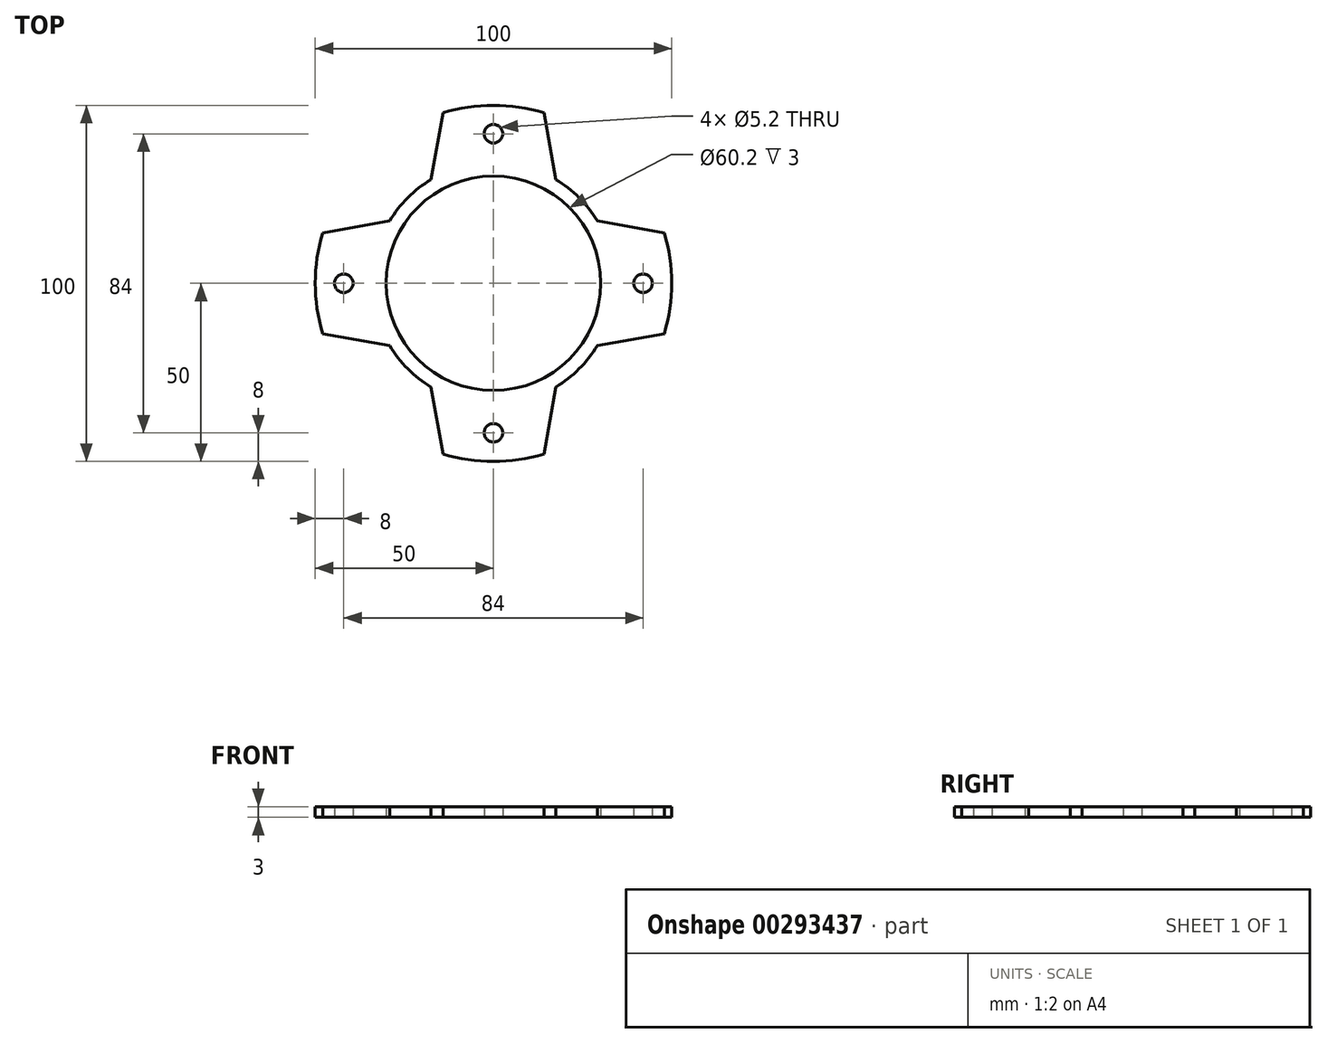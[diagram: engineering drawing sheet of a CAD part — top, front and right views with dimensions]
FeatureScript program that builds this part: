
annotation { "Feature Type Name" : "Feature", "Feature Type Description" : "" }
export const myFeature = defineFeature(function(context is Context, id is Id, definition is map)
    precondition{}
    {
        {
            var Q0;
            Q0=qCreatedBy(makeId("Top.planeOp"),FACE);
            var sketch = newSketch(context, id + "F0", { "sketchPlane" : qUnion([Q0])});
            skCircle(sketch, "E0", {"center": v(0, 0) * mm, "radius": 30.1 * mm});
            skCircle(sketch, "E1", {"center": v(0, 0) * mm, "radius": 34 * mm});
            skCircle(sketch, "E2", {"center": v(0, 0) * mm, "radius": 50 * mm});
            skCircle(sketch, "E3", {"center": v(-42, 0) * mm, "radius": 2.6 * mm});
            skCircle(sketch, "E4", {"center": v(42, 0) * mm, "radius": 2.6 * mm});
            skCircle(sketch, "E5", {"center": v(0, 42) * mm, "radius": 2.6 * mm});
            skCircle(sketch, "E6", {"center": v(0, -42) * mm, "radius": 2.6 * mm});
            skCircle(sketch, "E7", {"center": v(-42, 0) * mm, "radius": 15 * mm});
            skCircle(sketch, "E8", {"center": v(0, 42) * mm, "radius": 15 * mm});
            skCircle(sketch, "E9", {"center": v(42, 0) * mm, "radius": 15 * mm});
            skCircle(sketch, "E10", {"center": v(0, -42) * mm, "radius": 15 * mm});
            skLineSegment(sketch, "E11", {"start": v(-17.5, -29.15) * mm, "end": v(-10.6, -68.26) * mm});
            skLineSegment(sketch, "E12", {"start": v(-29.15, 17.5) * mm, "end": v(-64.19, 11.32) * mm});
            skLineSegment(sketch, "E13", {"start": v(-29.15, -17.5) * mm, "end": v(-69.22, -10.43) * mm});
            skLineSegment(sketch, "E14", {"start": v(-17.5, 29.15) * mm, "end": v(-10.72, 67.6) * mm});
            skLineSegment(sketch, "E15", {"start": v(29.15, 17.5) * mm, "end": v(70.35, 10.23) * mm});
            skLineSegment(sketch, "E16", {"start": v(29.15, -17.5) * mm, "end": v(61.9, -11.72) * mm});
            skLineSegment(sketch, "E17", {"start": v(17.5, -29.15) * mm, "end": v(11.2, -64.88) * mm});
            skLineSegment(sketch, "E18", {"start": v(17.5, 29.15) * mm, "end": v(10.52, 68.74) * mm});
            skSolve(sketch);
        }
        {
            var Q0;
            {var subQ5=sQuery(id+"F0.wireOp",EDGE,"E8");var subQ6=sQuery(id+"F0.wireOp",EDGE,"E0");var subQ7=makeQuery(id+"F0.imprint","INTERSECT",VERTEX,{"disambiguationData":[OD(1.0)],"derivedFrom":[subQ6,subQ5]});Q0=makeQuery(id+"F0.imprint","IMPRINT",FACE,{"disambiguationData":[TD([[makeQuery(id+"F0.imprint","IMPRINT",EDGE,{"disambiguationData":[TD([[subQ7,-1.0]])],"derivedFrom":subQ6}),-1.0]])]});}
            var Q1;
            {var subQ0=sQuery(id+"F0.wireOp",EDGE,"E14");var subQ1=sQuery(id+"F0.wireOp",EDGE,"E1");var subQ2=makeQuery(id+"F0.imprint","INTERSECT",VERTEX,{"derivedFrom":[subQ1,subQ0]});Q1=makeQuery(id+"F0.imprint","IMPRINT",FACE,{"disambiguationData":[TD([[makeQuery(id+"F0.imprint","IMPRINT",EDGE,{"disambiguationData":[TD([[subQ2,1.0]])],"derivedFrom":subQ1}),-1.0]])]});}
            var Q2;
            Q2=makeQuery(id+"F0.imprint","IMPRINT",FACE,{"disambiguationData":[TD([[makeQuery(id+"F0.imprint","IMPRINT",EDGE,{"derivedFrom":sQuery(id+"F0.wireOp",EDGE,"E5")}),-1.0]])]});
            var Q3;
            {var subQ0=sQuery(id+"F0.wireOp",EDGE,"E18");var subQ1=sQuery(id+"F0.wireOp",EDGE,"E1");var subQ2=makeQuery(id+"F0.imprint","INTERSECT",VERTEX,{"derivedFrom":[subQ1,subQ0]});Q3=makeQuery(id+"F0.imprint","IMPRINT",FACE,{"disambiguationData":[TD([[makeQuery(id+"F0.imprint","IMPRINT",EDGE,{"disambiguationData":[TD([[subQ2,-1.0]])],"derivedFrom":subQ1}),-1.0]])]});}
            var Q4;
            {var subQ0=sQuery(id+"F0.wireOp",EDGE,"E8");var subQ1=sQuery(id+"F0.wireOp",EDGE,"E0");var subQ2=makeQuery(id+"F0.imprint","INTERSECT",VERTEX,{"disambiguationData":[OD(0.0)],"derivedFrom":[subQ1,subQ0]});Q4=makeQuery(id+"F0.imprint","IMPRINT",FACE,{"disambiguationData":[TD([[makeQuery(id+"F0.imprint","IMPRINT",EDGE,{"disambiguationData":[TD([[subQ2,-1.0]])],"derivedFrom":subQ1}),-1.0]])]});}
            var Q5;
            {var subQ5=sQuery(id+"F0.wireOp",EDGE,"E8");var subQ7=sQuery(id+"F0.wireOp",EDGE,"E0");var subQ8=makeQuery(id+"F0.imprint","INTERSECT",VERTEX,{"disambiguationData":[OD(0.0)],"derivedFrom":[subQ7,subQ5]});Q5=makeQuery(id+"F0.imprint","IMPRINT",FACE,{"disambiguationData":[TD([[makeQuery(id+"F0.imprint","IMPRINT",EDGE,{"disambiguationData":[TD([[subQ8,1.0]])],"derivedFrom":subQ7}),-1.0]])]});}
            var Q6;
            {var subQ0=sQuery(id+"F0.wireOp",EDGE,"E15");var subQ1=sQuery(id+"F0.wireOp",EDGE,"E1");var subQ2=makeQuery(id+"F0.imprint","INTERSECT",VERTEX,{"derivedFrom":[subQ1,subQ0]});Q6=makeQuery(id+"F0.imprint","IMPRINT",FACE,{"disambiguationData":[TD([[makeQuery(id+"F0.imprint","IMPRINT",EDGE,{"disambiguationData":[TD([[subQ2,1.0]])],"derivedFrom":subQ1}),-1.0]])]});}
            var Q7;
            Q7=makeQuery(id+"F0.imprint","IMPRINT",FACE,{"disambiguationData":[TD([[makeQuery(id+"F0.imprint","IMPRINT",EDGE,{"derivedFrom":sQuery(id+"F0.wireOp",EDGE,"E4")}),-1.0]])]});
            var Q8;
            {var subQ0=sQuery(id+"F0.wireOp",EDGE,"E14");var subQ1=sQuery(id+"F0.wireOp",EDGE,"E2");var subQ2=makeQuery(id+"F0.imprint","INTERSECT",VERTEX,{"derivedFrom":[subQ1,subQ0]});Q8=makeQuery(id+"F0.imprint","IMPRINT",FACE,{"disambiguationData":[TD([[makeQuery(id+"F0.imprint","IMPRINT",EDGE,{"disambiguationData":[TD([[subQ2,1.0]])],"derivedFrom":subQ1}),1.0]])]});}
            var Q9;
            {var subQ0=sQuery(id+"F0.wireOp",EDGE,"E18");var subQ1=sQuery(id+"F0.wireOp",EDGE,"E2");var subQ2=makeQuery(id+"F0.imprint","INTERSECT",VERTEX,{"derivedFrom":[subQ1,subQ0]});Q9=makeQuery(id+"F0.imprint","IMPRINT",FACE,{"disambiguationData":[TD([[makeQuery(id+"F0.imprint","IMPRINT",EDGE,{"disambiguationData":[TD([[subQ2,-1.0]])],"derivedFrom":subQ1}),1.0]])]});}
            var Q10;
            {var subQ0=sQuery(id+"F0.wireOp",EDGE,"E16");var subQ1=sQuery(id+"F0.wireOp",EDGE,"E1");var subQ2=makeQuery(id+"F0.imprint","INTERSECT",VERTEX,{"derivedFrom":[subQ1,subQ0]});Q10=makeQuery(id+"F0.imprint","IMPRINT",FACE,{"disambiguationData":[TD([[makeQuery(id+"F0.imprint","IMPRINT",EDGE,{"disambiguationData":[TD([[subQ2,-1.0]])],"derivedFrom":subQ1}),-1.0]])]});}
            var Q11;
            {var subQ5=sQuery(id+"F0.wireOp",EDGE,"E10");var subQ7=sQuery(id+"F0.wireOp",EDGE,"E0");var subQ9=makeQuery(id+"F0.imprint","INTERSECT",VERTEX,{"disambiguationData":[OD(1.0)],"derivedFrom":[subQ7,subQ5]});Q11=makeQuery(id+"F0.imprint","IMPRINT",FACE,{"disambiguationData":[TD([[makeQuery(id+"F0.imprint","IMPRINT",EDGE,{"disambiguationData":[TD([[subQ9,-1.0]])],"derivedFrom":subQ7}),-1.0]])]});}
            var Q12;
            {var subQ0=sQuery(id+"F0.wireOp",EDGE,"E9");var subQ1=sQuery(id+"F0.wireOp",EDGE,"E0");var subQ2=makeQuery(id+"F0.imprint","INTERSECT",VERTEX,{"disambiguationData":[OD(0.0)],"derivedFrom":[subQ1,subQ0]});Q12=makeQuery(id+"F0.imprint","IMPRINT",FACE,{"disambiguationData":[TD([[makeQuery(id+"F0.imprint","IMPRINT",EDGE,{"disambiguationData":[TD([[subQ2,1.0]])],"derivedFrom":subQ1}),-1.0]])]});}
            var Q13;
            {var subQ0=sQuery(id+"F0.wireOp",EDGE,"E16");var subQ1=sQuery(id+"F0.wireOp",EDGE,"E2");var subQ2=makeQuery(id+"F0.imprint","INTERSECT",VERTEX,{"derivedFrom":[subQ1,subQ0]});Q13=makeQuery(id+"F0.imprint","IMPRINT",FACE,{"disambiguationData":[TD([[makeQuery(id+"F0.imprint","IMPRINT",EDGE,{"disambiguationData":[TD([[subQ2,-1.0]])],"derivedFrom":subQ1}),1.0]])]});}
            var Q14;
            {var subQ0=sQuery(id+"F0.wireOp",EDGE,"E15");var subQ1=sQuery(id+"F0.wireOp",EDGE,"E2");var subQ2=makeQuery(id+"F0.imprint","INTERSECT",VERTEX,{"derivedFrom":[subQ1,subQ0]});Q14=makeQuery(id+"F0.imprint","IMPRINT",FACE,{"disambiguationData":[TD([[makeQuery(id+"F0.imprint","IMPRINT",EDGE,{"disambiguationData":[TD([[subQ2,1.0]])],"derivedFrom":subQ1}),1.0]])]});}
            var Q15;
            {var subQ0=sQuery(id+"F0.wireOp",EDGE,"E10");var subQ1=sQuery(id+"F0.wireOp",EDGE,"E0");var subQ2=makeQuery(id+"F0.imprint","INTERSECT",VERTEX,{"disambiguationData":[OD(0.0)],"derivedFrom":[subQ1,subQ0]});Q15=makeQuery(id+"F0.imprint","IMPRINT",FACE,{"disambiguationData":[TD([[makeQuery(id+"F0.imprint","IMPRINT",EDGE,{"disambiguationData":[TD([[subQ2,-1.0]])],"derivedFrom":subQ1}),-1.0]])]});}
            var Q16;
            Q16=makeQuery(id+"F0.imprint","IMPRINT",FACE,{"disambiguationData":[TD([[makeQuery(id+"F0.imprint","IMPRINT",EDGE,{"derivedFrom":sQuery(id+"F0.wireOp",EDGE,"E6")}),-1.0]])]});
            var Q17;
            {var subQ0=sQuery(id+"F0.wireOp",EDGE,"E11");var subQ1=sQuery(id+"F0.wireOp",EDGE,"E1");var subQ2=makeQuery(id+"F0.imprint","INTERSECT",VERTEX,{"derivedFrom":[subQ1,subQ0]});Q17=makeQuery(id+"F0.imprint","IMPRINT",FACE,{"disambiguationData":[TD([[makeQuery(id+"F0.imprint","IMPRINT",EDGE,{"disambiguationData":[TD([[subQ2,-1.0]])],"derivedFrom":subQ1}),-1.0]])]});}
            var Q18;
            {var subQ5=sQuery(id+"F0.wireOp",EDGE,"E7");var subQ6=sQuery(id+"F0.wireOp",EDGE,"E0");var subQ7=makeQuery(id+"F0.imprint","INTERSECT",VERTEX,{"disambiguationData":[OD(1.0)],"derivedFrom":[subQ6,subQ5]});Q18=makeQuery(id+"F0.imprint","IMPRINT",FACE,{"disambiguationData":[TD([[makeQuery(id+"F0.imprint","IMPRINT",EDGE,{"disambiguationData":[TD([[subQ7,-1.0]])],"derivedFrom":subQ6}),-1.0]])]});}
            var Q19;
            {var subQ0=sQuery(id+"F0.wireOp",EDGE,"E17");var subQ1=sQuery(id+"F0.wireOp",EDGE,"E1");var subQ2=makeQuery(id+"F0.imprint","INTERSECT",VERTEX,{"derivedFrom":[subQ1,subQ0]});Q19=makeQuery(id+"F0.imprint","IMPRINT",FACE,{"disambiguationData":[TD([[makeQuery(id+"F0.imprint","IMPRINT",EDGE,{"disambiguationData":[TD([[subQ2,1.0]])],"derivedFrom":subQ1}),-1.0]])]});}
            var Q20;
            {var subQ0=sQuery(id+"F0.wireOp",EDGE,"E17");var subQ1=sQuery(id+"F0.wireOp",EDGE,"E2");var subQ2=makeQuery(id+"F0.imprint","INTERSECT",VERTEX,{"derivedFrom":[subQ1,subQ0]});Q20=makeQuery(id+"F0.imprint","IMPRINT",FACE,{"disambiguationData":[TD([[makeQuery(id+"F0.imprint","IMPRINT",EDGE,{"disambiguationData":[TD([[subQ2,1.0]])],"derivedFrom":subQ1}),1.0]])]});}
            var Q21;
            {var subQ0=sQuery(id+"F0.wireOp",EDGE,"E11");var subQ1=sQuery(id+"F0.wireOp",EDGE,"E2");var subQ2=makeQuery(id+"F0.imprint","INTERSECT",VERTEX,{"derivedFrom":[subQ1,subQ0]});Q21=makeQuery(id+"F0.imprint","IMPRINT",FACE,{"disambiguationData":[TD([[makeQuery(id+"F0.imprint","IMPRINT",EDGE,{"disambiguationData":[TD([[subQ2,-1.0]])],"derivedFrom":subQ1}),1.0]])]});}
            var Q22;
            Q22=makeQuery(id+"F0.imprint","IMPRINT",FACE,{"disambiguationData":[TD([[makeQuery(id+"F0.imprint","IMPRINT",EDGE,{"derivedFrom":sQuery(id+"F0.wireOp",EDGE,"E3")}),-1.0]])]});
            var Q23;
            {var subQ0=sQuery(id+"F0.wireOp",EDGE,"E13");var subQ1=sQuery(id+"F0.wireOp",EDGE,"E1");var subQ2=makeQuery(id+"F0.imprint","INTERSECT",VERTEX,{"derivedFrom":[subQ1,subQ0]});Q23=makeQuery(id+"F0.imprint","IMPRINT",FACE,{"disambiguationData":[TD([[makeQuery(id+"F0.imprint","IMPRINT",EDGE,{"disambiguationData":[TD([[subQ2,1.0]])],"derivedFrom":subQ1}),-1.0]])]});}
            var Q24;
            {var subQ0=sQuery(id+"F0.wireOp",EDGE,"E7");var subQ1=sQuery(id+"F0.wireOp",EDGE,"E0");var subQ2=makeQuery(id+"F0.imprint","INTERSECT",VERTEX,{"disambiguationData":[OD(0.0)],"derivedFrom":[subQ1,subQ0]});Q24=makeQuery(id+"F0.imprint","IMPRINT",FACE,{"disambiguationData":[TD([[makeQuery(id+"F0.imprint","IMPRINT",EDGE,{"disambiguationData":[TD([[subQ2,-1.0]])],"derivedFrom":subQ1}),-1.0]])]});}
            var Q25;
            {var subQ0=sQuery(id+"F0.wireOp",EDGE,"E12");var subQ1=sQuery(id+"F0.wireOp",EDGE,"E1");var subQ2=makeQuery(id+"F0.imprint","INTERSECT",VERTEX,{"derivedFrom":[subQ1,subQ0]});Q25=makeQuery(id+"F0.imprint","IMPRINT",FACE,{"disambiguationData":[TD([[makeQuery(id+"F0.imprint","IMPRINT",EDGE,{"disambiguationData":[TD([[subQ2,-1.0]])],"derivedFrom":subQ1}),-1.0]])]});}
            var Q26;
            {var subQ0=sQuery(id+"F0.wireOp",EDGE,"E12");var subQ1=sQuery(id+"F0.wireOp",EDGE,"E2");var subQ2=makeQuery(id+"F0.imprint","INTERSECT",VERTEX,{"derivedFrom":[subQ1,subQ0]});Q26=makeQuery(id+"F0.imprint","IMPRINT",FACE,{"disambiguationData":[TD([[makeQuery(id+"F0.imprint","IMPRINT",EDGE,{"disambiguationData":[TD([[subQ2,-1.0]])],"derivedFrom":subQ1}),1.0]])]});}
            var Q27;
            {var subQ0=sQuery(id+"F0.wireOp",EDGE,"E13");var subQ1=sQuery(id+"F0.wireOp",EDGE,"E2");var subQ2=makeQuery(id+"F0.imprint","INTERSECT",VERTEX,{"derivedFrom":[subQ1,subQ0]});Q27=makeQuery(id+"F0.imprint","IMPRINT",FACE,{"disambiguationData":[TD([[makeQuery(id+"F0.imprint","IMPRINT",EDGE,{"disambiguationData":[TD([[subQ2,1.0]])],"derivedFrom":subQ1}),1.0]])]});}
            extrude(context, id + "F1", {"entities" : qUnion([Q0, Q1, Q2, Q3, Q4, Q5, Q6, Q7, Q8, Q9, Q10, Q11, Q12, Q13, Q14, Q15, Q16, Q17, Q18, Q19, Q20, Q21, Q22, Q23, Q24, Q25, Q26, Q27]), "depth" : 3 * mm, "offsetDistance" : 25 * mm});
        }
    });
